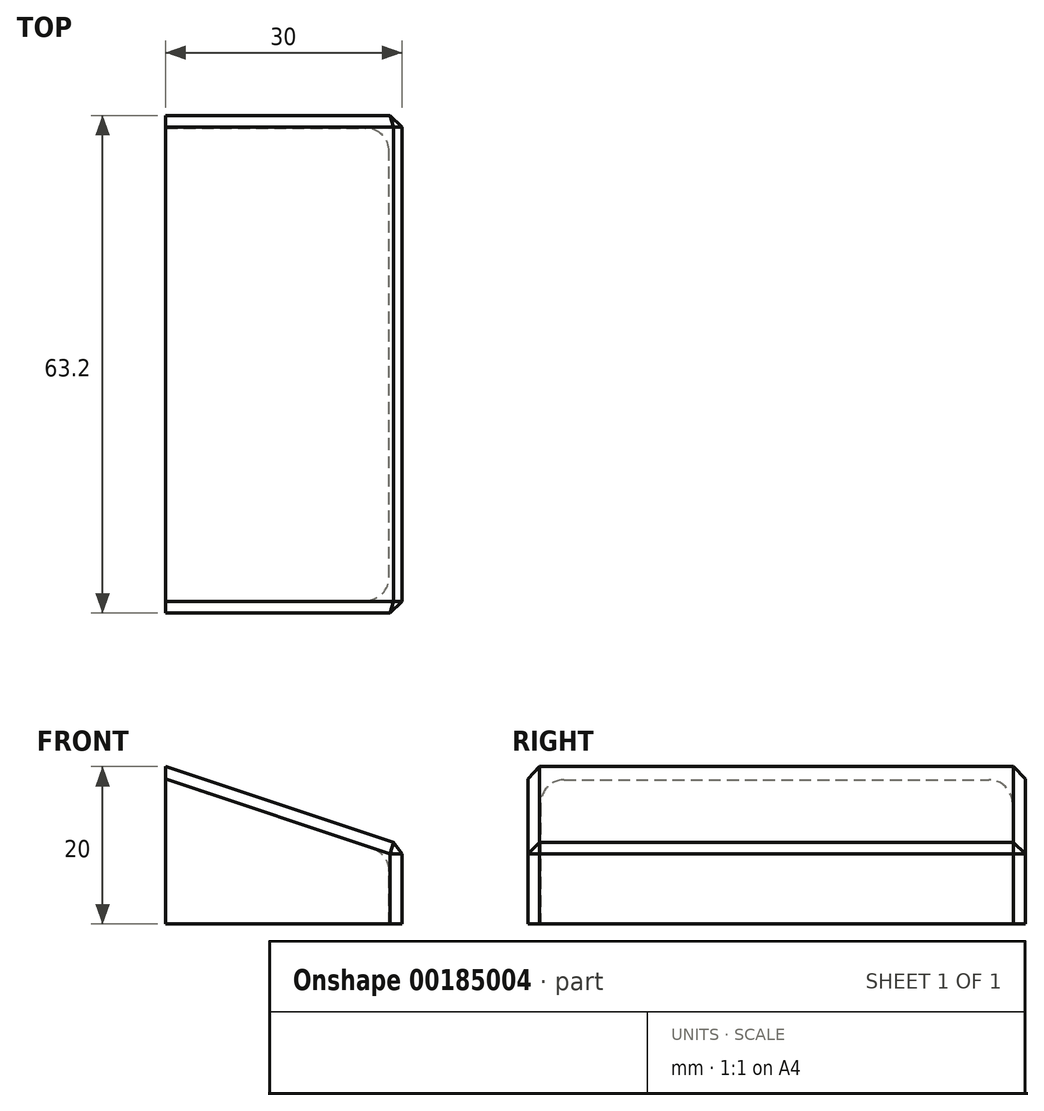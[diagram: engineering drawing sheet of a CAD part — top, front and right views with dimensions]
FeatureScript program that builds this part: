
annotation { "Feature Type Name" : "Feature", "Feature Type Description" : "" }
export const myFeature = defineFeature(function(context is Context, id is Id, definition is map)
    precondition{}
    {
        {
            var Q0;
            Q0=qCreatedBy(makeId("Front.planeOp"),FACE);
            var sketch = newSketch(context, id + "F0", { "sketchPlane" : qUnion([Q0])});
            skLineSegment(sketch, "E0", {"start": v(0, 0) * mm, "end": v(30, 0) * mm});
            skLineSegment(sketch, "E1", {"start": v(30, 0) * mm, "end": v(30, 10) * mm});
            skLineSegment(sketch, "E2", {"start": v(30, 10) * mm, "end": v(0, 20) * mm});
            skLineSegment(sketch, "E3", {"start": v(0, 20) * mm, "end": v(0, 0) * mm});
            skSolve(sketch);
        }
        {
            var Q0;
            Q0 = qSketchRegion(id + "F0", true);
            extrude(context, id + "F1", {"entities" : qUnion([Q0]), "endBound" : BoundingType.SYMMETRIC, "depth" : 63.2 * mm});
        }
        {
            var Q0;
            Q0=makeQuery(id+"F1.opExtrude","SWEPT_FACE",FACE,{"disambiguationData":[OSD([sQuery(id+"F0.wireOp",EDGE,"E3")])]});
            var Q1;
            Q1=makeQuery(id+"F1.opExtrude","SWEPT_FACE",FACE,{"disambiguationData":[OSD([sQuery(id+"F0.wireOp",EDGE,"E0")])]});
            shell(context, id + "F2", {"entities" : qUnion([Q0, Q1]), "thickness" : 1.6 * mm});
        }
        {
            var Q0;
            {var subQ0=sQuery(id+"F0.wireOp",EDGE,"E2");Q0=makeQuery(id+"F2.opShell","OFFSET_EDGE",EDGE,{"disambiguationData":[OSD([subQ0]),TDD([makeQuery(id+"F1.opExtrude","CAP_EDGE",EDGE,{"disambiguationData":[OSD([subQ0])],"isStart":true})])]});}
            var Q1;
            {var subQ0=sQuery(id+"F0.wireOp",EDGE,"E2");Q1=makeQuery(id+"F2.opShell","OFFSET_EDGE",EDGE,{"disambiguationData":[OSD([subQ0]),TDD([makeQuery(id+"F1.opExtrude","CAP_EDGE",EDGE,{"disambiguationData":[OSD([subQ0])],"isStart":false})])]});}
            var Q2;
            Q2=makeQuery(id+"F2.opShell","OFFSET_EDGE",EDGE,{"disambiguationData":[OSD([sQuery(id+"F0.wireOp",EDGE,"E1"),sQuery(id+"F0.wireOp",EDGE,"E2")])]});
            var Q3;
            {var subQ0=sQuery(id+"F0.wireOp",EDGE,"E1");Q3=makeQuery(id+"F2.opShell","OFFSET_EDGE",EDGE,{"disambiguationData":[OSD([subQ0]),TDD([makeQuery(id+"F1.opExtrude","CAP_EDGE",EDGE,{"disambiguationData":[OSD([subQ0])],"isStart":false})])]});}
            var Q4;
            {var subQ0=sQuery(id+"F0.wireOp",EDGE,"E1");Q4=makeQuery(id+"F2.opShell","OFFSET_EDGE",EDGE,{"disambiguationData":[OSD([subQ0]),TDD([makeQuery(id+"F1.opExtrude","CAP_EDGE",EDGE,{"disambiguationData":[OSD([subQ0])],"isStart":true})])]});}
            fillet(context, id + "F3", {"entities" : qUnion([Q0, Q1, Q2, Q3, Q4]), "radius" : 3 * mm, "tangentPropagation" : true, "allowEdgeOverflow" : false});
        }
        {
            var Q0;
            Q0=makeQuery(id+"F1.opExtrude","SWEPT_EDGE",EDGE,{"disambiguationData":[OSD([sQuery(id+"F0.wireOp",EDGE,"E1"),sQuery(id+"F0.wireOp",EDGE,"E2")])]});
            var Q1;
            Q1=makeQuery(id+"F1.opExtrude","CAP_EDGE",EDGE,{"disambiguationData":[OSD([sQuery(id+"F0.wireOp",EDGE,"E1")])],"isStart":false});
            var Q2;
            Q2=makeQuery(id+"F1.opExtrude","CAP_EDGE",EDGE,{"disambiguationData":[OSD([sQuery(id+"F0.wireOp",EDGE,"E1")])],"isStart":true});
            var Q3;
            Q3=makeQuery(id+"F1.opExtrude","CAP_EDGE",EDGE,{"disambiguationData":[OSD([sQuery(id+"F0.wireOp",EDGE,"E2")])],"isStart":true});
            var Q4;
            Q4=makeQuery(id+"F1.opExtrude","CAP_EDGE",EDGE,{"disambiguationData":[OSD([sQuery(id+"F0.wireOp",EDGE,"E2")])],"isStart":false});
            chamfer(context, id + "F4", {"entities" : qUnion([Q0, Q1, Q2, Q3, Q4]), "width" : 1.5 * mm, "tangentPropagation" : true});
        }
    });
